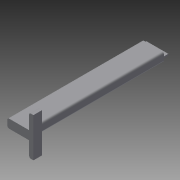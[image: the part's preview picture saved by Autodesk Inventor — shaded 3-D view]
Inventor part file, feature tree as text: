
AUTODESK INVENTOR PART (.ipt)
format: ipt  version: 2015 (Build 190159000, 159)  size: 125,952 bytes
history: native  units: mm
features: extrude x3, fillet x3, sketch x3
ambient origin geometry x8: Origin, YZ Plane, XZ Plane, XY Plane, X Axis, Y Axis, Z Axis, Center Point
bodies: Solid1 (feature_tree)
feature tree (9):
  extrude  "Extrusion1"  Depth=30.0mm
  extrude  "Extrusion2"  Depth=10.0mm
  fillet  "Fillet1"  Radius=17.5mm
  extrude  "Extrusion3"  Depth=10.0mm TaperAngle=0.0deg
  fillet  "Fillet2"  Radius=145.0mm
  fillet  "Fillet3"  Radius=2.0mm
  sketch  "Sketch1"  dims[d0=45.0mm d1=30.0mm]
  sketch  "Sketch2"  dims[d2=10.0mm d3=17.5mm d4=17.5mm]
  sketch  "Sketch3"  dims[d5=5.0mm d6=10.0mm d7=0.0mm d8=145.0mm d9=0.0mm d10=2.0mm d11=2.0mm d12=4.0mm d13=4.0mm d14=5.0mm d15=0.0mm d16=2.0mm d17=2.0mm]
